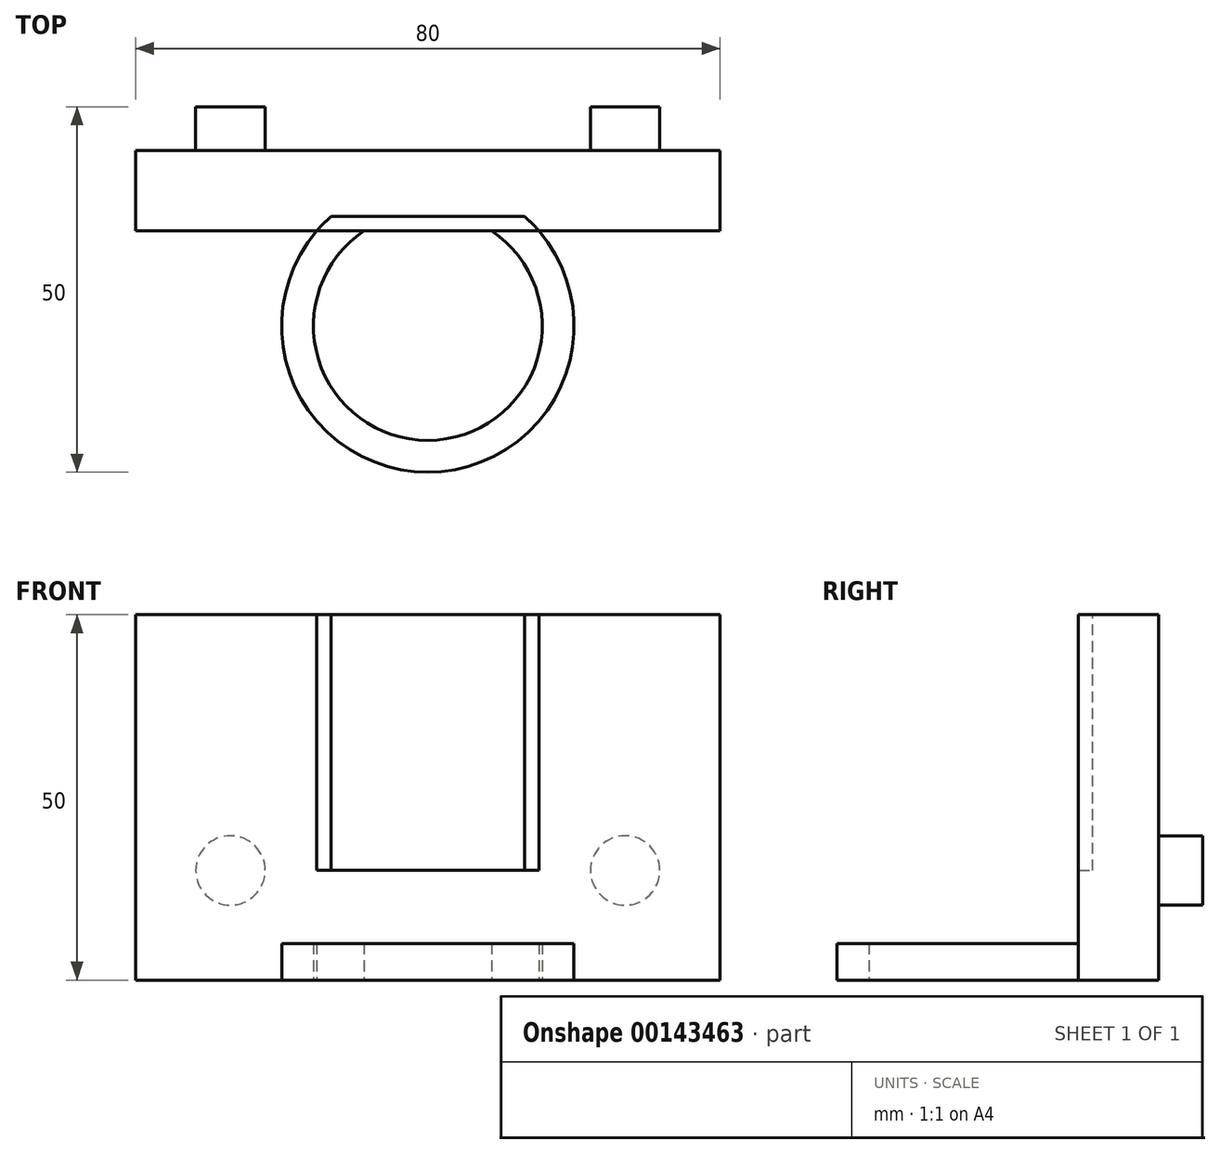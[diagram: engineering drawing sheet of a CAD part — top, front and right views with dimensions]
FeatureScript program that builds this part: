
annotation { "Feature Type Name" : "Feature", "Feature Type Description" : "" }
export const myFeature = defineFeature(function(context is Context, id is Id, definition is map)
    precondition{}
    {
        {
            var Q0;
            Q0=qCreatedBy(makeId("Front.planeOp"),FACE);
            var sketch = newSketch(context, id + "F0", { "sketchPlane" : qUnion([Q0])});
            skCircle(sketch, "E0", {"center": v(-27, 0) * mm, "radius": 4.75 * mm});
            skCircle(sketch, "E1", {"center": v(27, 0) * mm, "radius": 4.75 * mm});
            skSolve(sketch);
        }
        {
            var Q0;
            Q0=makeQuery(id+"F0.imprint","IMPRINT",FACE,{"disambiguationData":[TD([[makeQuery(id+"F0.imprint","IMPRINT",EDGE,{"derivedFrom":sQuery(id+"F0.wireOp",EDGE,"E0")}),1.0]])]});
            var Q1;
            Q1=makeQuery(id+"F0.imprint","IMPRINT",FACE,{"disambiguationData":[TD([[makeQuery(id+"F0.imprint","IMPRINT",EDGE,{"derivedFrom":sQuery(id+"F0.wireOp",EDGE,"E1")}),1.0]])]});
            extrude(context, id + "F1", {"entities" : qUnion([Q0, Q1]), "depth" : 6 * mm});
        }
        {
            var Q0;
            Q0=makeQuery(id+"F1.opExtrude","CAP_FACE",FACE,{"disambiguationData":[OSD([sQuery(id+"F0.wireOp",EDGE,"E0")])],"isStart":false});
            var sketch = newSketch(context, id + "F2", { "sketchPlane" : qUnion([Q0])});
            skLineSegment(sketch, "E2.top", {"start": v(40, -15) * mm, "end": v(-40, -15) * mm});
            skLineSegment(sketch, "E2.left", {"start": v(40, 15) * mm, "end": v(40, -15) * mm});
            skLineSegment(sketch, "E2.right", {"start": v(-40, 15) * mm, "end": v(-40, -15) * mm});
            skPoint(sketch, "E2.middle", {"position": v(0, 0) * mm});
            skLineSegment(sketch, "E3", {"start": v(-40, 15) * mm, "end": v(-40, 35) * mm});
            skLineSegment(sketch, "E4", {"start": v(40, 15) * mm, "end": v(40, 35) * mm});
            skLineSegment(sketch, "E5", {"start": v(40, 35) * mm, "end": v(-40, 35) * mm});
            skSolve(sketch);
        }
        {
            var Q0;
            Q0=makeQuery(id+"F2.imprint","IMPRINT",FACE,{"disambiguationData":[TD([[makeQuery(id+"F2.imprint","IMPRINT",EDGE,{"derivedFrom":makeQuery(id+"F1.opExtrude","CAP_EDGE",EDGE,{"disambiguationData":[OSD([sQuery(id+"F0.wireOp",EDGE,"E0")])],"isStart":false})}),1.0]])]});
            var Q1;
            Q1=makeQuery(id+"F2.imprint","IMPRINT",FACE,{"disambiguationData":[TD([[makeQuery(id+"F2.imprint","IMPRINT",EDGE,{"derivedFrom":sQuery(id+"F2.wireOp",EDGE,"E2.top")}),-1.0]])]});
            extrude(context, id + "F3", {"entities" : qUnion([Q0, Q1]), "depth" : 11 * mm});
        }
        {
            var Q0;
            Q0=makeQuery(id+"F3.opExtrude","SWEPT_FACE",FACE,{"disambiguationData":[OSD([sQuery(id+"F2.wireOp",EDGE,"E2.top")])]});
            var sketch = newSketch(context, id + "F4", { "sketchPlane" : qUnion([Q0])});
            skCircle(sketch, "E6", {"center": v(0, 30) * mm, "radius": 15.65 * mm});
            skLineSegment(sketch, "E7.0.0", {"start": v(-40, 6) * mm, "end": v(40, 6) * mm});
            skLineSegment(sketch, "E7.0.1", {"start": v(40, 6) * mm, "end": v(40, 17) * mm});
            skLineSegment(sketch, "E7.0.2", {"start": v(40, 17) * mm, "end": v(-40, 17) * mm});
            skLineSegment(sketch, "E7.0.3", {"start": v(-40, 17) * mm, "end": v(-40, 6) * mm});
            skCircle(sketch, "E8", {"center": v(0, 30) * mm, "radius": 20 * mm});
            skSolve(sketch);
        }
        {
            var Q0;
            {var subQ0=sQuery(id+"F4.wireOp",EDGE,"E7.0.2");var subQ1=sQuery(id+"F4.wireOp",EDGE,"E6");var subQ2=makeQuery(id+"F4.imprint","INTERSECT",VERTEX,{"disambiguationData":[OD(0.0)],"derivedFrom":[subQ1,subQ0]});Q0=makeQuery(id+"F4.imprint","IMPRINT",FACE,{"disambiguationData":[TD([[makeQuery(id+"F4.imprint","IMPRINT",EDGE,{"disambiguationData":[TD([[subQ2,-1.0]])],"derivedFrom":subQ1}),-1.0]])]});}
            extrude(context, id + "F5", {"entities" : qUnion([Q0]), "operationType" : NewBodyOperationType.ADD, "oppositeDirection" : true, "depth" : 5 * mm});
        }
        {
            var Q0;
            Q0=makeQuery(id+"F3.opExtrude","SWEPT_FACE",FACE,{"disambiguationData":[OSD([sQuery(id+"F2.wireOp",EDGE,"E5")])]});
            var sketch = newSketch(context, id + "F6", { "sketchPlane" : qUnion([Q0])});
            skLineSegment(sketch, "E9.0.0", {"start": v(40, -6) * mm, "end": v(-40, -6) * mm});
            skLineSegment(sketch, "E9.0.1", {"start": v(-40, -6) * mm, "end": v(-40, -17) * mm});
            skLineSegment(sketch, "E9.0.2", {"start": v(-40, -17) * mm, "end": v(40, -17) * mm});
            skLineSegment(sketch, "E9.0.3", {"start": v(40, -17) * mm, "end": v(40, -6) * mm});
            skArc(sketch, "E10.0", {"start": v(8.71, -17) * mm, "mid": v(0, -45.65) * mm, "end": v(-8.71, -17) * mm});
            skArc(sketch, "E11.0", {"start": v(15.2, -17) * mm, "mid": v(0, -50) * mm, "end": v(-15.2, -17) * mm});
            skCircle(sketch, "E12", {"center": v(0, -30) * mm, "radius": 20 * mm});
            skLineSegment(sketch, "E13.bottom", {"start": v(13.25, -15.02) * mm, "end": v(-13.25, -15.02) * mm});
            skLineSegment(sketch, "E13.top", {"start": v(13.25, -44.98) * mm, "end": v(-13.25, -44.98) * mm});
            skLineSegment(sketch, "E13.left", {"start": v(13.25, -15.02) * mm, "end": v(13.25, -44.98) * mm});
            skLineSegment(sketch, "E13.right", {"start": v(-13.25, -15.02) * mm, "end": v(-13.25, -44.98) * mm});
            skSolve(sketch);
        }
        {
            var Q0;
            {var subQ0=sQuery(id+"F6.wireOp",EDGE,"E12");var subQ1=sQuery(id+"F6.wireOp",EDGE,"E9.0.2");var subQ2=makeQuery(id+"F6.imprint","INTERSECT",VERTEX,{"disambiguationData":[OD(1.0)],"derivedFrom":[subQ1,subQ0]});Q0=makeQuery(id+"F6.imprint","IMPRINT",FACE,{"disambiguationData":[TD([[makeQuery(id+"F6.imprint","IMPRINT",EDGE,{"disambiguationData":[TD([[subQ2,1.0]])],"derivedFrom":subQ1}),-1.0]])]});}
            var Q1;
            {var subQ0=sQuery(id+"F6.wireOp",EDGE,"E13.bottom");Q1=makeQuery(id+"F6.imprint","IMPRINT",FACE,{"disambiguationData":[TD([[makeQuery(id+"F6.imprint","IMPRINT",EDGE,{"derivedFrom":subQ0}),1.0]])]});}
            var Q2;
            {var subQ0=sQuery(id+"F6.wireOp",EDGE,"E12");var subQ1=sQuery(id+"F6.wireOp",EDGE,"E9.0.2");var subQ2=makeQuery(id+"F6.imprint","INTERSECT",VERTEX,{"disambiguationData":[OD(0.0)],"derivedFrom":[subQ1,subQ0]});Q2=makeQuery(id+"F6.imprint","IMPRINT",FACE,{"disambiguationData":[TD([[makeQuery(id+"F6.imprint","IMPRINT",EDGE,{"disambiguationData":[TD([[subQ2,-1.0]])],"derivedFrom":subQ1}),-1.0]])]});}
            extrude(context, id + "F7", {"entities" : qUnion([Q0, Q1, Q2]), "operationType" : NewBodyOperationType.REMOVE, "oppositeDirection" : true, "depth" : 35 * mm});
        }
    });
